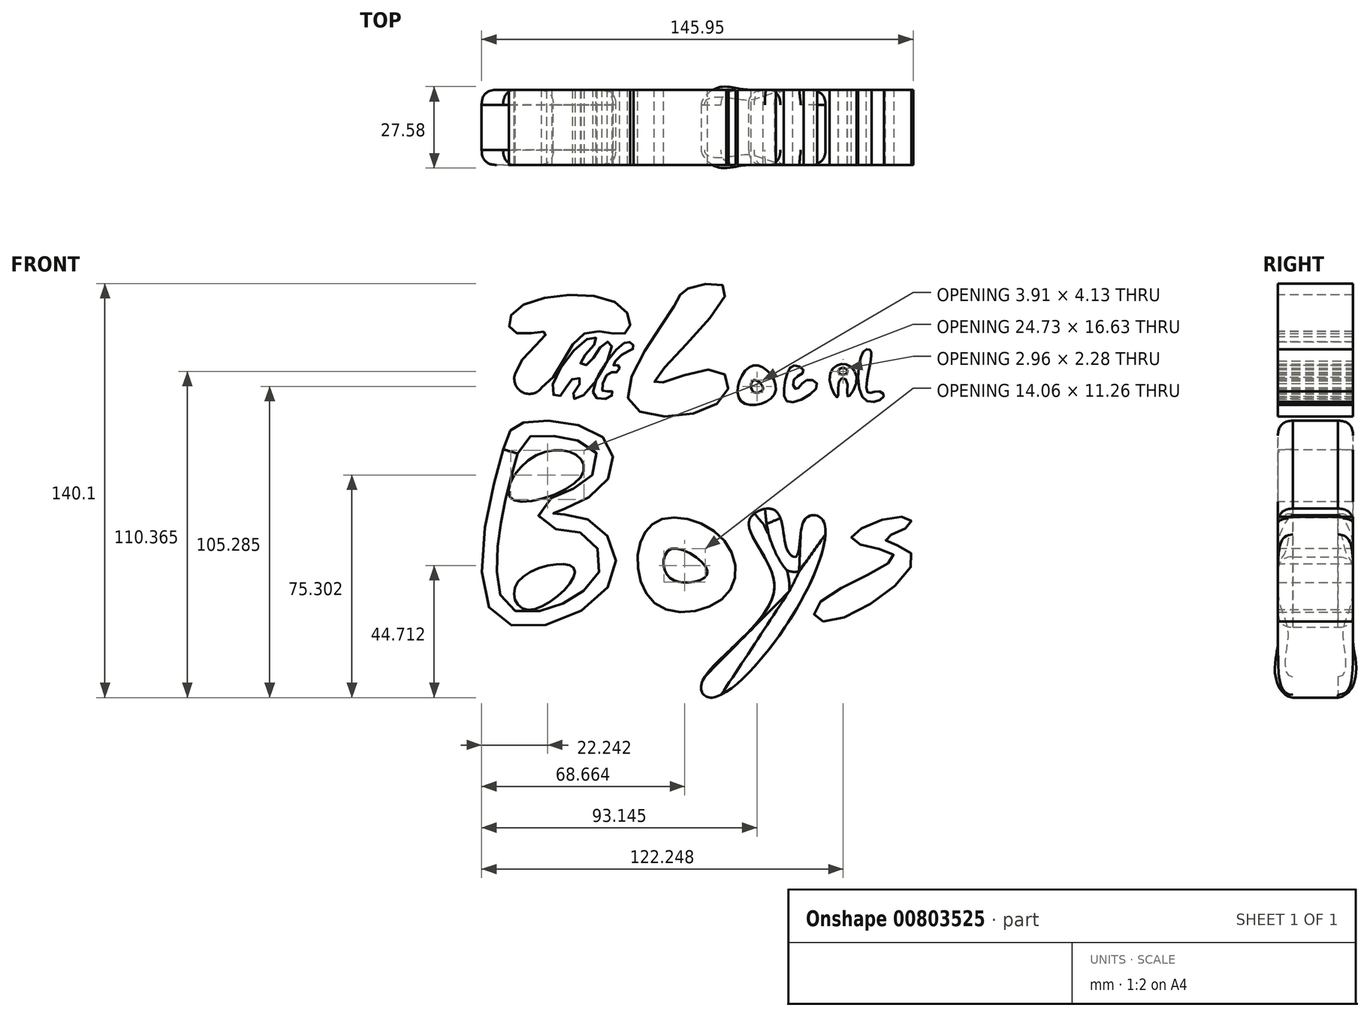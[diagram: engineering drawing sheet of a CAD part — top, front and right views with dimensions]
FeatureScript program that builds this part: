
annotation { "Feature Type Name" : "Feature", "Feature Type Description" : "" }
export const myFeature = defineFeature(function(context is Context, id is Id, definition is map)
    precondition{}
    {
        {
            var Q0;
            Q0=qCreatedBy(makeId("Front.planeOp"),FACE);
            var sketch = newSketch(context, id + "F0", { "sketchPlane" : qUnion([Q0])});
            skArc(sketch, "E0", {"start": v(-61.01, 42.42) * mm, "mid": v(-58.63, 36.1) * mm, "end": v(-52.06, 37.6) * mm});
            skFitSpline(sketch, "E1", {"points": [v(-61.01, 42.42) * mm, v(-50.45, 56.2) * mm, v(-61.01, 56.2) * mm, v(-61.01, 63.77) * mm, v(-25.43, 65.37) * mm, v(-23.59, 56.2) * mm, v(-37.6, 55.96) * mm, v(-52.06, 37.6) * mm, v(-61.01, 42.42) * mm]});
            skSolve(sketch);
        }
        {
            var Q0;
            {var subQ0=sQuery(id+"F0.wireOp",EDGE,"E0");Q0=makeQuery(id+"F0.imprint","IMPRINT",FACE,{"disambiguationData":[TD([[makeQuery(id+"F0.imprint","IMPRINT",EDGE,{"derivedFrom":subQ0}),1.0]])]});}
            var Q1;
            {var subQ0=sQuery(id+"F0.wireOp",EDGE,"E1");var subQ1=sQuery(id+"F0.wireOp",EDGE,"E0");var subQ2=makeQuery(id+"F0.imprint","INTERSECT",VERTEX,{"disambiguationData":[OD(0.0)],"derivedFrom":[subQ1,subQ0]});Q1=makeQuery(id+"F0.imprint","IMPRINT",FACE,{"disambiguationData":[TD([[makeQuery(id+"F0.imprint","IMPRINT",EDGE,{"disambiguationData":[TD([[subQ2,-1.0]])],"derivedFrom":subQ0}),-1.0]])]});}
            extrude(context, id + "F1", {"entities" : qUnion([Q0, Q1]), "depth" : 25.4 * mm, "offsetDistance" : 25.4 * mm});
        }
        {
            var Q0;
            Q0=qCreatedBy(makeId("Front.planeOp"),FACE);
            var sketch = newSketch(context, id + "F2", { "sketchPlane" : qUnion([Q0])});
            skFitSpline(sketch, "E2", {"points": [v(-48.61, 36.45) * mm, v(-36.22, 54.35) * mm, v(-33.46, 53.67) * mm, v(-38.97, 46.09) * mm, v(-36.68, 45.4) * mm, v(-31.17, 52.52) * mm, v(-28.41, 52.29) * mm, v(-39.2, 34.15) * mm, v(-41.73, 34.84) * mm, v(-38.74, 40.12) * mm, v(-41.73, 40.58) * mm, v(-45.86, 34.84) * mm, v(-48.61, 36.45) * mm]});
            skFitSpline(sketch, "E3", {"points": [v(-25.66, 51.6) * mm, v(-34.38, 34.84) * mm, v(-28.41, 34.84) * mm, v(-28.41, 36.45) * mm, v(-31.4, 36.45) * mm, v(-29.33, 42.65) * mm, v(-26.57, 42.87) * mm, v(-25.89, 45.17) * mm, v(-27.72, 45.17) * mm, v(-24.5, 49.07) * mm, v(-21.06, 50.91) * mm, v(-21.75, 52.75) * mm, v(-25.66, 51.6) * mm]});
            skSolve(sketch);
        }
        {
            var Q0;
            {var subQ0=sQuery(id+"F2.wireOp",EDGE,"E3");var subQ1=sQuery(id+"F2.wireOp",EDGE,"E2");var subQ2=makeQuery(id+"F2.imprint","INTERSECT",VERTEX,{"disambiguationData":[OD(0.0)],"derivedFrom":[subQ1,subQ0]});Q0=makeQuery(id+"F2.imprint","IMPRINT",FACE,{"disambiguationData":[TD([[makeQuery(id+"F2.imprint","IMPRINT",EDGE,{"disambiguationData":[TD([[subQ2,-1.0]])],"derivedFrom":subQ1}),-1.0]])]});}
            var Q1;
            {var subQ0=sQuery(id+"F2.wireOp",EDGE,"E3");var subQ1=sQuery(id+"F2.wireOp",EDGE,"E2");var subQ2=makeQuery(id+"F2.imprint","INTERSECT",VERTEX,{"disambiguationData":[OD(0.0)],"derivedFrom":[subQ1,subQ0]});Q1=makeQuery(id+"F2.imprint","IMPRINT",FACE,{"disambiguationData":[TD([[makeQuery(id+"F2.imprint","IMPRINT",EDGE,{"disambiguationData":[TD([[subQ2,1.0]])],"derivedFrom":subQ1}),1.0]])]});}
            extrude(context, id + "F3", {"entities" : qUnion([Q0, Q1]), "depth" : 25.4 * mm, "offsetDistance" : 25.4 * mm});
        }
        {
            var Q0;
            Q0=qCreatedBy(makeId("Front.planeOp"),FACE);
            var sketch = newSketch(context, id + "F4", { "sketchPlane" : qUnion([Q0])});
            skFitSpline(sketch, "E4", {"points": [v(-7.29, 65.14) * mm, v(-22.21, 32.31) * mm, v(9.01, 33.7) * mm, v(6.94, 43.56) * mm, v(-13.95, 39.43) * mm, v(10.39, 70.65) * mm, v(-2.7, 71.11) * mm, v(-7.29, 65.14) * mm]});
            skFitSpline(sketch, "E5", {"points": [v(19.57, 45.17) * mm, v(15.2, 33.23) * mm, v(26.92, 35.99) * mm, v(19.57, 45.17) * mm]});
            skFitSpline(sketch, "E6", {"points": [v(19.57, 40.12) * mm, v(19.57, 36.22) * mm, v(22.79, 37.36) * mm, v(19.57, 40.12) * mm]});
            skFitSpline(sketch, "E7", {"points": [v(33.35, 45.17) * mm, v(30.36, 40.12) * mm, v(31.51, 32.77) * mm, v(41.15, 38.28) * mm, v(37.48, 40.12) * mm, v(34.04, 37.14) * mm, v(33.12, 40.12) * mm, v(36.56, 43.1) * mm, v(33.35, 45.17) * mm]});
            skFitSpline(sketch, "E8", {"points": [v(47.81, 45.17) * mm, v(45.29, 40.12) * mm, v(48.04, 34.38) * mm, v(48.73, 40.12) * mm, v(51.03, 40.12) * mm, v(51.48, 34.6) * mm, v(54.47, 40.12) * mm, v(51.71, 45.17) * mm, v(47.81, 45.17) * mm]});
            skFitSpline(sketch, "E9", {"points": [v(48.73, 43.9) * mm, v(48.73, 42.3) * mm, v(51.03, 42.42) * mm, v(51.03, 43.9) * mm, v(48.73, 43.9) * mm]});
            skSolve(sketch);
        }
        {
            var Q0;
            Q0=makeQuery(id+"F4.imprint","IMPRINT",FACE,{"disambiguationData":[TD([[makeQuery(id+"F4.imprint","IMPRINT",EDGE,{"derivedFrom":sQuery(id+"F4.wireOp",EDGE,"E9")}),1.0]])]});
            var sketch = newSketch(context, id + "F5", { "sketchPlane" : qUnion([Q0])});
            skFitSpline(sketch, "E10", {"points": [v(56.76, 49.87) * mm, v(57.3, 33.45) * mm, v(63.65, 34.77) * mm, v(61.53, 36.36) * mm, v(58.09, 36.1) * mm, v(59.41, 48.02) * mm, v(58.88, 50.4) * mm, v(56.76, 49.87) * mm]});
            skSolve(sketch);
        }
        {
            var Q0;
            Q0=makeQuery(id+"F4.imprint","IMPRINT",FACE,{"disambiguationData":[TD([[makeQuery(id+"F4.imprint","IMPRINT",EDGE,{"derivedFrom":sQuery(id+"F4.wireOp",EDGE,"E4")}),1.0]])]});
            var Q1;
            Q1=makeQuery(id+"F4.imprint","IMPRINT",FACE,{"disambiguationData":[TD([[makeQuery(id+"F4.imprint","IMPRINT",EDGE,{"derivedFrom":sQuery(id+"F4.wireOp",EDGE,"E5")}),1.0]])]});
            var Q2;
            Q2=makeQuery(id+"F4.imprint","IMPRINT",FACE,{"disambiguationData":[TD([[makeQuery(id+"F4.imprint","IMPRINT",EDGE,{"derivedFrom":sQuery(id+"F4.wireOp",EDGE,"E7")}),1.0]])]});
            var Q3;
            Q3=makeQuery(id+"F4.imprint","IMPRINT",FACE,{"disambiguationData":[TD([[makeQuery(id+"F4.imprint","IMPRINT",EDGE,{"derivedFrom":sQuery(id+"F4.wireOp",EDGE,"E8")}),1.0]])]});
            var Q4;
            Q4=makeQuery(id+"F5.imprint","IMPRINT",FACE,{"disambiguationData":[TD([[makeQuery(id+"F5.imprint","IMPRINT",EDGE,{"derivedFrom":sQuery(id+"F5.wireOp",EDGE,"E10")}),1.0]])]});
            extrude(context, id + "F6", {"entities" : qUnion([Q0, Q1, Q2, Q3, Q4]), "depth" : 25.4 * mm, "offsetDistance" : 25.4 * mm});
        }
        {
            var Q0;
            Q0=qCreatedBy(makeId("Front.planeOp"),FACE);
            var sketch = newSketch(context, id + "F7", { "sketchPlane" : qUnion([Q0])});
            skFitSpline(sketch, "E11", {"points": [v(-65.1, 16.76) * mm, v(-67.23, -40.2) * mm, v(-28.81, -28.55) * mm, v(-36.23, -7.09) * mm, v(-48.15, -4.97) * mm, v(-32.52, 3.25) * mm, v(-30.93, 20.47) * mm, v(-58.48, 25.76) * mm, v(-65.1, 16.76) * mm]});
            skFitSpline(sketch, "E12", {"points": [v(-11.33, -6.82) * mm, v(-19.54, -19) * mm, v(-11.6, -36.76) * mm, v(10.93, -32) * mm, v(9.34, -13.71) * mm, v(-11.33, -6.82) * mm]});
            skFitSpline(sketch, "E13", {"points": [v(-8.15, -16.89) * mm, v(-10.27, -24.57) * mm, v(-3.11, -28.28) * mm, v(4.04, -24.57) * mm, v(-8.15, -16.89) * mm]});
            skFitSpline(sketch, "E14", {"points": [v(18.08, -7.62) * mm, v(26.56, -30.93) * mm, v(2.19, -61.93) * mm, v(5.1, -67.23) * mm, v(34.24, -37.02) * mm, v(42.72, -6.82) * mm, v(36.9, -7.09) * mm, v(34.24, -19.27) * mm, v(31.06, -17.42) * mm, v(26.82, -3.9) * mm, v(18.08, -7.62) * mm]});
            skFitSpline(sketch, "E15", {"points": [v(69.74, -6.03) * mm, v(52.79, -13.71) * mm, v(67.1, -19.27) * mm, v(40.87, -36.23) * mm, v(44.31, -41.53) * mm, v(73.45, -19.54) * mm, v(64.18, -13.71) * mm, v(72.66, -8.68) * mm, v(69.74, -6.03) * mm]});
            skSolve(sketch);
        }
        {
            var Q0;
            Q0 = qSketchRegion(id + "F7", true);
            extrude(context, id + "F8", {"entities" : qUnion([Q0]), "depth" : 25.4 * mm, "offsetDistance" : 25.4 * mm});
        }
        {
            var Q0;
            Q0=makeQuery(id+"F1.opExtrude","CAP_EDGE",EDGE,{"disambiguationData":[OSD([sQuery(id+"F0.wireOp",EDGE,"E1")])],"isStart":true});
            var Q1;
            Q1=makeQuery(id+"F1.opExtrude","CAP_EDGE",EDGE,{"disambiguationData":[OSD([sQuery(id+"F0.wireOp",EDGE,"E1")])],"isStart":false});
            var Q2;
            {var subQ0=sQuery(id+"F2.wireOp",EDGE,"E3");var subQ1=sQuery(id+"F2.wireOp",EDGE,"E2");Q2=makeQuery(id+"F3.opExtrude","CAP_EDGE",EDGE,{"disambiguationData":[OSD([subQ1]),TDD([makeQuery(id+"F2.imprint","IMPRINT",EDGE,{"disambiguationData":[TD([[makeQuery(id+"F2.imprint","INTERSECT",VERTEX,{"disambiguationData":[OD(0.0)],"derivedFrom":[subQ1,subQ0]}),1.0]])],"derivedFrom":subQ1})])],"isStart":false});}
            var Q3;
            {var subQ0=sQuery(id+"F2.wireOp",EDGE,"E3");var subQ1=sQuery(id+"F2.wireOp",EDGE,"E2");Q3=makeQuery(id+"F3.opExtrude","CAP_EDGE",EDGE,{"disambiguationData":[OSD([subQ0]),TDD([makeQuery(id+"F2.imprint","IMPRINT",EDGE,{"disambiguationData":[TD([[makeQuery(id+"F2.imprint","INTERSECT",VERTEX,{"disambiguationData":[OD(0.0)],"derivedFrom":[subQ1,subQ0]}),-1.0]])],"derivedFrom":subQ0})])],"isStart":false});}
            var Q4;
            {var subQ0=sQuery(id+"F2.wireOp",EDGE,"E3");var subQ1=sQuery(id+"F2.wireOp",EDGE,"E2");Q4=makeQuery(id+"F3.opExtrude","CAP_EDGE",EDGE,{"disambiguationData":[OSD([subQ1]),TDD([makeQuery(id+"F2.imprint","IMPRINT",EDGE,{"disambiguationData":[TD([[makeQuery(id+"F2.imprint","INTERSECT",VERTEX,{"disambiguationData":[OD(0.0)],"derivedFrom":[subQ1,subQ0]}),-1.0]])],"derivedFrom":subQ1})])],"isStart":false});}
            var Q5;
            {var subQ0=sQuery(id+"F2.wireOp",EDGE,"E3");var subQ1=sQuery(id+"F2.wireOp",EDGE,"E2");Q5=makeQuery(id+"F3.opExtrude","CAP_EDGE",EDGE,{"disambiguationData":[OSD([subQ0]),TDD([makeQuery(id+"F2.imprint","IMPRINT",EDGE,{"disambiguationData":[TD([[makeQuery(id+"F2.imprint","INTERSECT",VERTEX,{"disambiguationData":[OD(0.0)],"derivedFrom":[subQ1,subQ0]}),1.0]])],"derivedFrom":subQ0})])],"isStart":false});}
            var Q6;
            Q6=makeQuery(id+"F6.opExtrude","CAP_EDGE",EDGE,{"disambiguationData":[OSD([sQuery(id+"F4.wireOp",EDGE,"E4")])],"isStart":true});
            var Q7;
            Q7=makeQuery(id+"F6.opExtrude","CAP_EDGE",EDGE,{"disambiguationData":[OSD([sQuery(id+"F4.wireOp",EDGE,"E4")])],"isStart":false});
            var Q8;
            Q8=makeQuery(id+"F6.opExtrude","CAP_EDGE",EDGE,{"disambiguationData":[OSD([sQuery(id+"F4.wireOp",EDGE,"E5")])],"isStart":true});
            var Q9;
            Q9=makeQuery(id+"F6.opExtrude","CAP_EDGE",EDGE,{"disambiguationData":[OSD([sQuery(id+"F4.wireOp",EDGE,"E5")])],"isStart":false});
            var Q10;
            Q10=makeQuery(id+"F6.opExtrude","CAP_EDGE",EDGE,{"disambiguationData":[OSD([sQuery(id+"F4.wireOp",EDGE,"E7")])],"isStart":false});
            var Q11;
            Q11=makeQuery(id+"F6.opExtrude","CAP_EDGE",EDGE,{"disambiguationData":[OSD([sQuery(id+"F5.wireOp",EDGE,"E10")])],"isStart":false});
            var Q12;
            Q12=makeQuery(id+"F6.opExtrude","CAP_EDGE",EDGE,{"disambiguationData":[OSD([sQuery(id+"F5.wireOp",EDGE,"E10")])],"isStart":true});
            var Q13;
            Q13=makeQuery(id+"F8.opExtrude","CAP_EDGE",EDGE,{"disambiguationData":[OSD([sQuery(id+"F7.wireOp",EDGE,"E11")])],"isStart":true});
            var Q14;
            Q14=makeQuery(id+"F8.opExtrude","CAP_EDGE",EDGE,{"disambiguationData":[OSD([sQuery(id+"F7.wireOp",EDGE,"E12")])],"isStart":true});
            var Q15;
            Q15=makeQuery(id+"F8.opExtrude","CAP_EDGE",EDGE,{"disambiguationData":[OSD([sQuery(id+"F7.wireOp",EDGE,"E12")])],"isStart":false});
            var Q16;
            Q16=makeQuery(id+"F8.opExtrude","CAP_EDGE",EDGE,{"disambiguationData":[OSD([sQuery(id+"F7.wireOp",EDGE,"E13")])],"isStart":false});
            var Q17;
            Q17=makeQuery(id+"F8.opExtrude","CAP_EDGE",EDGE,{"disambiguationData":[OSD([sQuery(id+"F7.wireOp",EDGE,"E14")])],"isStart":true});
            var Q18;
            Q18=makeQuery(id+"F8.opExtrude","CAP_EDGE",EDGE,{"disambiguationData":[OSD([sQuery(id+"F7.wireOp",EDGE,"E14")])],"isStart":false});
            var Q19;
            Q19=makeQuery(id+"F8.opExtrude","CAP_EDGE",EDGE,{"disambiguationData":[OSD([sQuery(id+"F7.wireOp",EDGE,"E15")])],"isStart":false});
            var Q20;
            {var subQ0=sQuery(id+"F0.wireOp",EDGE,"E1");var subQ1=sQuery(id+"F0.wireOp",EDGE,"E0");Q20=makeQuery(id+"F1.opExtrude","SWEPT_EDGE",EDGE,{"disambiguationData":[OSD([subQ1,subQ0]),TDD([makeQuery(id+"F0.imprint","INTERSECT",VERTEX,{"disambiguationData":[OD(0.0)],"derivedFrom":[subQ1,subQ0]})])]});}
            var Q21;
            {var subQ0=sQuery(id+"F0.wireOp",EDGE,"E1");var subQ1=sQuery(id+"F0.wireOp",EDGE,"E0");Q21=makeQuery(id+"F1.opExtrude","SWEPT_EDGE",EDGE,{"disambiguationData":[OSD([subQ1,subQ0]),TDD([makeQuery(id+"F0.imprint","INTERSECT",VERTEX,{"disambiguationData":[OD(1.0)],"derivedFrom":[subQ1,subQ0]})])]});}
            var Q22;
            Q22=makeQuery(id+"F1.opExtrude","CAP_EDGE",EDGE,{"disambiguationData":[OSD([sQuery(id+"F0.wireOp",EDGE,"E0")])],"isStart":true});
            var Q23;
            Q23=makeQuery(id+"F1.opExtrude","CAP_EDGE",EDGE,{"disambiguationData":[OSD([sQuery(id+"F0.wireOp",EDGE,"E0")])],"isStart":false});
            var Q24;
            {var subQ0=sQuery(id+"F2.wireOp",EDGE,"E3");var subQ1=sQuery(id+"F2.wireOp",EDGE,"E2");Q24=makeQuery(id+"F3.opExtrude","CAP_EDGE",EDGE,{"disambiguationData":[OSD([subQ1]),TDD([makeQuery(id+"F2.imprint","IMPRINT",EDGE,{"disambiguationData":[TD([[makeQuery(id+"F2.imprint","INTERSECT",VERTEX,{"disambiguationData":[OD(0.0)],"derivedFrom":[subQ1,subQ0]}),1.0]])],"derivedFrom":subQ1})])],"isStart":true});}
            var Q25;
            {var subQ0=sQuery(id+"F2.wireOp",EDGE,"E3");var subQ1=sQuery(id+"F2.wireOp",EDGE,"E2");Q25=makeQuery(id+"F3.opExtrude","CAP_EDGE",EDGE,{"disambiguationData":[OSD([subQ0]),TDD([makeQuery(id+"F2.imprint","IMPRINT",EDGE,{"disambiguationData":[TD([[makeQuery(id+"F2.imprint","INTERSECT",VERTEX,{"disambiguationData":[OD(0.0)],"derivedFrom":[subQ1,subQ0]}),-1.0]])],"derivedFrom":subQ0})])],"isStart":true});}
            var Q26;
            {var subQ0=sQuery(id+"F2.wireOp",EDGE,"E3");var subQ1=sQuery(id+"F2.wireOp",EDGE,"E2");Q26=makeQuery(id+"F3.opExtrude","SWEPT_EDGE",EDGE,{"disambiguationData":[OSD([subQ1,subQ0]),TDD([makeQuery(id+"F2.imprint","INTERSECT",VERTEX,{"disambiguationData":[OD(0.0)],"derivedFrom":[subQ1,subQ0]})]),OD(0.0)]});}
            var Q27;
            {var subQ0=sQuery(id+"F2.wireOp",EDGE,"E3");var subQ1=sQuery(id+"F2.wireOp",EDGE,"E2");Q27=makeQuery(id+"F3.opExtrude","SWEPT_EDGE",EDGE,{"disambiguationData":[OSD([subQ1,subQ0]),TDD([makeQuery(id+"F2.imprint","INTERSECT",VERTEX,{"disambiguationData":[OD(1.0)],"derivedFrom":[subQ1,subQ0]})]),OD(0.0)]});}
            var Q28;
            {var subQ0=sQuery(id+"F2.wireOp",EDGE,"E3");var subQ1=sQuery(id+"F2.wireOp",EDGE,"E2");Q28=makeQuery(id+"F3.opExtrude","CAP_EDGE",EDGE,{"disambiguationData":[OSD([subQ1]),TDD([makeQuery(id+"F2.imprint","IMPRINT",EDGE,{"disambiguationData":[TD([[makeQuery(id+"F2.imprint","INTERSECT",VERTEX,{"disambiguationData":[OD(0.0)],"derivedFrom":[subQ1,subQ0]}),-1.0]])],"derivedFrom":subQ1})])],"isStart":true});}
            var Q29;
            Q29=makeQuery(id+"F6.opExtrude","CAP_EDGE",EDGE,{"disambiguationData":[OSD([sQuery(id+"F4.wireOp",EDGE,"E6")])],"isStart":true});
            var Q30;
            Q30=makeQuery(id+"F6.opExtrude","CAP_EDGE",EDGE,{"disambiguationData":[OSD([sQuery(id+"F4.wireOp",EDGE,"E6")])],"isStart":false});
            var Q31;
            Q31=makeQuery(id+"F6.opExtrude","CAP_EDGE",EDGE,{"disambiguationData":[OSD([sQuery(id+"F4.wireOp",EDGE,"E7")])],"isStart":true});
            var Q32;
            Q32=makeQuery(id+"F6.opExtrude","CAP_EDGE",EDGE,{"disambiguationData":[OSD([sQuery(id+"F4.wireOp",EDGE,"E8")])],"isStart":true});
            var Q33;
            Q33=makeQuery(id+"F6.opExtrude","CAP_EDGE",EDGE,{"disambiguationData":[OSD([sQuery(id+"F4.wireOp",EDGE,"E8")])],"isStart":false});
            var Q34;
            Q34=makeQuery(id+"F6.opExtrude","CAP_EDGE",EDGE,{"disambiguationData":[OSD([sQuery(id+"F4.wireOp",EDGE,"E9")])],"isStart":true});
            var Q35;
            Q35=makeQuery(id+"F6.opExtrude","CAP_EDGE",EDGE,{"disambiguationData":[OSD([sQuery(id+"F4.wireOp",EDGE,"E9")])],"isStart":false});
            var Q36;
            Q36=makeQuery(id+"F8.opExtrude","CAP_EDGE",EDGE,{"disambiguationData":[OSD([sQuery(id+"F7.wireOp",EDGE,"E13")])],"isStart":true});
            var Q37;
            {var subQ0=sQuery(id+"F2.wireOp",EDGE,"E3");var subQ1=sQuery(id+"F2.wireOp",EDGE,"E2");Q37=makeQuery(id+"F3.opExtrude","CAP_EDGE",EDGE,{"disambiguationData":[OSD([subQ0]),TDD([makeQuery(id+"F2.imprint","IMPRINT",EDGE,{"disambiguationData":[TD([[makeQuery(id+"F2.imprint","INTERSECT",VERTEX,{"disambiguationData":[OD(0.0)],"derivedFrom":[subQ1,subQ0]}),1.0]])],"derivedFrom":subQ0})])],"isStart":true});}
            var Q38;
            {var subQ0=sQuery(id+"F2.wireOp",EDGE,"E3");var subQ1=sQuery(id+"F2.wireOp",EDGE,"E2");Q38=makeQuery(id+"F3.opExtrude","SWEPT_EDGE",EDGE,{"disambiguationData":[OSD([subQ1,subQ0]),TDD([makeQuery(id+"F2.imprint","INTERSECT",VERTEX,{"disambiguationData":[OD(0.0)],"derivedFrom":[subQ1,subQ0]})]),OD(1.0)]});}
            var Q39;
            {var subQ0=sQuery(id+"F2.wireOp",EDGE,"E3");var subQ1=sQuery(id+"F2.wireOp",EDGE,"E2");Q39=makeQuery(id+"F3.opExtrude","SWEPT_EDGE",EDGE,{"disambiguationData":[OSD([subQ1,subQ0]),TDD([makeQuery(id+"F2.imprint","INTERSECT",VERTEX,{"disambiguationData":[OD(1.0)],"derivedFrom":[subQ1,subQ0]})]),OD(1.0)]});}
            var Q40;
            Q40=makeQuery(id+"F8.opExtrude","CAP_EDGE",EDGE,{"disambiguationData":[OSD([sQuery(id+"F7.wireOp",EDGE,"E11")])],"isStart":false});
            var Q41;
            Q41=makeQuery(id+"F8.opExtrude","CAP_EDGE",EDGE,{"disambiguationData":[OSD([sQuery(id+"F7.wireOp",EDGE,"E15")])],"isStart":true});
            fillet(context, id + "F9", {"entities" : qUnion([Q0, Q1, Q2, Q3, Q4, Q5, Q6, Q7, Q8, Q9, Q10, Q11, Q12, Q13, Q14, Q15, Q16, Q17, Q18, Q19, Q20, Q21, Q22, Q23, Q24, Q25, Q26, Q27, Q28, Q29, Q30, Q31, Q32, Q33, Q34, Q35, Q36, Q37, Q38, Q39, Q40, Q41]), "radius" : 5.08 * mm, "tangentPropagation" : true, "rho" : 0.5, "crossSection" : FilletCrossSection.CONIC, "allowEdgeOverflow" : false});
        }
        {
            var Q0;
            Q0=makeQuery(id+"F8.opExtrude","CAP_FACE",FACE,{"disambiguationData":[OSD([sQuery(id+"F7.wireOp",EDGE,"E11")])],"isStart":false});
            var sketch = newSketch(context, id + "F10", { "sketchPlane" : qUnion([Q0])});
            skFitSpline(sketch, "E16", {"points": [v(-56.63, 13.05) * mm, v(-62.2, 0) * mm, v(-39.14, 6.95) * mm, v(-40.47, 14.9) * mm, v(-56.63, 13.05) * mm]});
            skFitSpline(sketch, "E17", {"points": [v(-60.07, -28.02) * mm, v(-56.63, -37.55) * mm, v(-41, -23.78) * mm, v(-60.07, -28.02) * mm]});
            skSolve(sketch);
        }
        {
            var Q0;
            Q0=makeQuery(id+"F10.imprint","IMPRINT",FACE,{"disambiguationData":[TD([[makeQuery(id+"F10.imprint","IMPRINT",EDGE,{"derivedFrom":sQuery(id+"F10.wireOp",EDGE,"E17")}),1.0]])]});
            var Q1;
            Q1=makeQuery(id+"F10.imprint","IMPRINT",FACE,{"disambiguationData":[TD([[makeQuery(id+"F10.imprint","IMPRINT",EDGE,{"derivedFrom":sQuery(id+"F10.wireOp",EDGE,"E16")}),1.0]])]});
            extrude(context, id + "F11", {"entities" : qUnion([Q0, Q1]), "operationType" : NewBodyOperationType.REMOVE, "oppositeDirection" : true, "depth" : 25.4 * mm, "offsetDistance" : 25.4 * mm});
        }
    });
